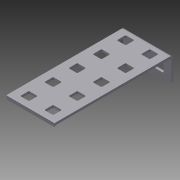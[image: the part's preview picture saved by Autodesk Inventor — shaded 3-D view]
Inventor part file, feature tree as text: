
AUTODESK INVENTOR PART (.ipt)
format: ipt  version: 2012 (Build 160160000, 160)  size: 1,956,864 bytes
history: native  units: in
note: dims shown in document units (in); Inventor stores cm internally (conversion verified against a paired STEP export)
features: sketch x7, extrude x2, other x1, imported_body x1, plane x1, split x1
ambient origin geometry x8: Origin, YZ Plane, XZ Plane, XY Plane, X Axis, Y Axis, Z Axis, Center Point
feature tree (13):
  parser-record x1  (decoder bookkeeping rows leaked as tree rows — omitted from the tree; the rows remain in map.json)
  imported_body  "Base1"
  sketch  "Sketch1"  dims[d0=5.9055in d2=0.5in d3=0.3937in d5=1.0in d7=5.9055in d9=0.5in d10=1.9685in d12=0.5in]
  sketch  "Sketch2"  dims[d15=0.5in d19=-1.0in]
  sketch  "Sketch3"  dims[d20=1.0in d21=0.0in]
  sketch  "Sketch4"  dims[d22=1.0in d23=0.0in]
  plane  "Work Plane1"
  split  "Split1"
  sketch  "Sketch5"
  extrude  "Extrusion1"  Depth=5.9055in
  extrude  "Extrusion2"  [1 undecoded]
  sketch  "Sketch6"
  sketch  "Sketch7"
note: 1 required parameter value undecoded (feature->parameter linkage not recoverable at this tier; creation-order binding heuristic only, values carry confidence <= 0.55)
